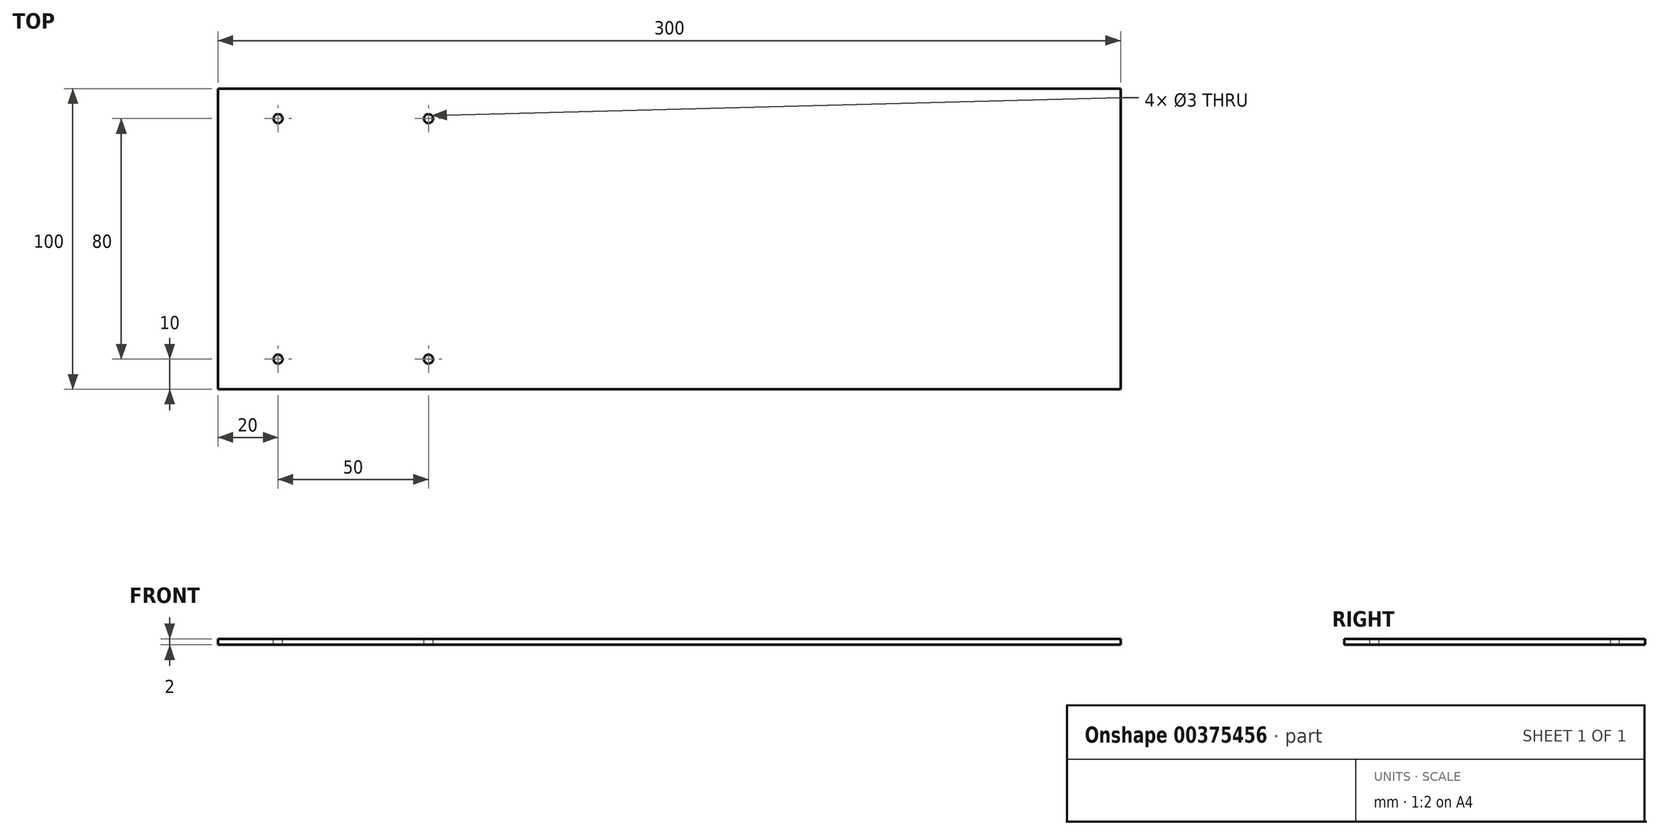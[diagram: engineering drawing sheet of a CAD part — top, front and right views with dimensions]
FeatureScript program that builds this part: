
annotation { "Feature Type Name" : "Feature", "Feature Type Description" : "" }
export const myFeature = defineFeature(function(context is Context, id is Id, definition is map)
    precondition{}
    {
        {
            var Q0;
            Q0=qCreatedBy(makeId("Top.planeOp"),FACE);
            var sketch = newSketch(context, id + "F0", { "sketchPlane" : qUnion([Q0])});
            skLineSegment(sketch, "E0.bottom", {"start": v(150, 50) * mm, "end": v(-150, 50) * mm});
            skLineSegment(sketch, "E0.top", {"start": v(150, -50) * mm, "end": v(-150, -50) * mm});
            skLineSegment(sketch, "E0.left", {"start": v(150, 50) * mm, "end": v(150, -50) * mm});
            skLineSegment(sketch, "E0.right", {"start": v(-150, 50) * mm, "end": v(-150, -50) * mm});
            skPoint(sketch, "E0.middle", {"position": v(0, 0) * mm});
            skSolve(sketch);
        }
        {
            var Q0;
            Q0=makeQuery(id+"F0.imprint","IMPRINT",FACE,{"disambiguationData":[TD([[makeQuery(id+"F0.imprint","IMPRINT",EDGE,{"derivedFrom":sQuery(id+"F0.wireOp",EDGE,"E0.bottom")}),1.0]])]});
            extrude(context, id + "F1", {"entities" : qUnion([Q0]), "depth" : 2 * mm, "offsetDistance" : 25.4 * mm});
        }
        {
            var Q0;
            Q0=makeQuery(id+"F1.opExtrude","CAP_FACE",FACE,{"disambiguationData":[OSD([sQuery(id+"F0.wireOp",EDGE,"E0.bottom"),sQuery(id+"F0.wireOp",EDGE,"E0.top"),sQuery(id+"F0.wireOp",EDGE,"E0.left"),sQuery(id+"F0.wireOp",EDGE,"E0.right")])],"isStart":false});
            var sketch = newSketch(context, id + "F2", { "sketchPlane" : qUnion([Q0])});
            skLineSegment(sketch, "E1", {"start": v(0, 0) * mm, "end": v(0, 37.85) * mm, "construction": true});
            skLineSegment(sketch, "E2", {"start": v(0, 0) * mm, "end": v(46.46, 0) * mm, "construction": true});
            skCircle(sketch, "E3", {"center": v(-130, 40) * mm, "radius": 1.5 * mm});
            skCircle(sketch, "E4", {"center": v(-80, 40) * mm, "radius": 1.5 * mm});
            skLineSegment(sketch, "E5", {"start": v(-130, 40) * mm, "end": v(-80, 40) * mm, "construction": true});
            skCircle(sketch, "E6.MirrorC", {"center": v(-80, -40) * mm, "radius": 1.5 * mm});
            skCircle(sketch, "E7.MirrorC", {"center": v(-130, -40) * mm, "radius": 1.5 * mm});
            skSolve(sketch);
        }
        {
            var Q0;
            Q0 = qSketchRegion(id + "F2", true);
            extrude(context, id + "F3", {"entities" : qUnion([Q0]), "operationType" : NewBodyOperationType.REMOVE, "oppositeDirection" : true, "depth" : 25.4 * mm, "offsetDistance" : 25.4 * mm});
        }
    });
